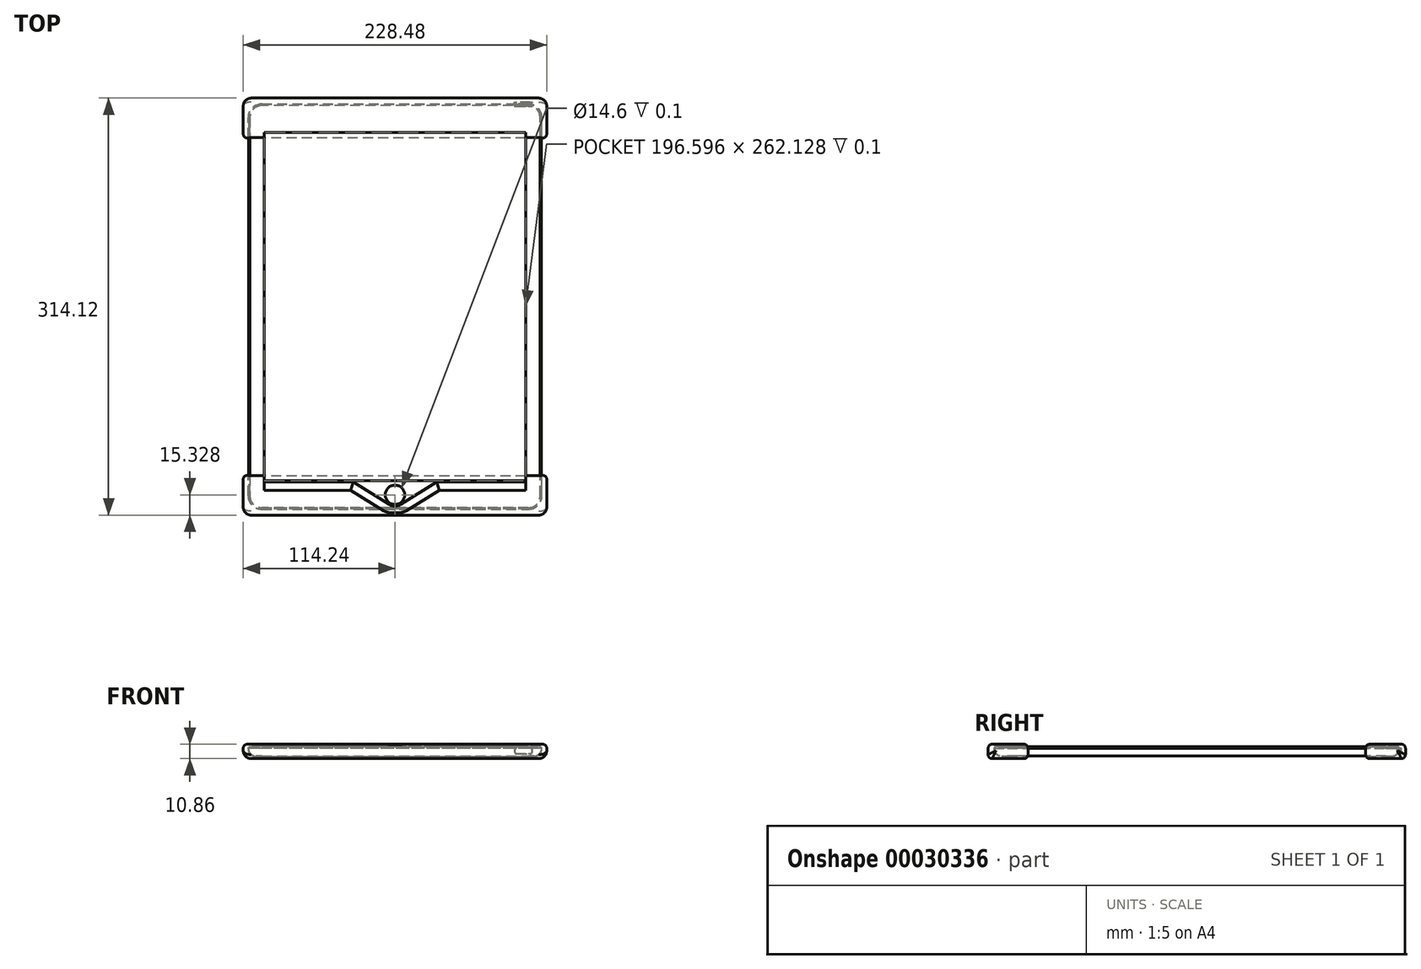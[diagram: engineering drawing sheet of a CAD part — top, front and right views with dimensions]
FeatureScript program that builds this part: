
annotation { "Feature Type Name" : "Feature", "Feature Type Description" : "" }
export const myFeature = defineFeature(function(context is Context, id is Id, definition is map)
    precondition{}
    {
        {
            var Q0;
            Q0=qCreatedBy(makeId("Top.planeOp"),FACE);
            var sketch = newSketch(context, id + "F0", { "sketchPlane" : qUnion([Q0])});
            skLineSegment(sketch, "E0.rect.bottom", {"start": v(-100.24, 152.4) * mm, "end": v(100.24, 152.4) * mm});
            skLineSegment(sketch, "E0.rect.top", {"start": v(-100.24, -152.4) * mm, "end": v(100.24, -152.4) * mm});
            skLineSegment(sketch, "E0.rect.left", {"start": v(-110.24, 142.4) * mm, "end": v(-110.24, -142.4) * mm});
            skLineSegment(sketch, "E0.rect.right", {"start": v(110.24, 142.4) * mm, "end": v(110.24, -142.4) * mm});
            skPoint(sketch, "E0.rect.middle", {"position": v(0, 0) * mm});
            skLineSegment(sketch, "E1.rect.bottom", {"start": v(98.3, 131.06) * mm, "end": v(-98.3, 131.06) * mm});
            skLineSegment(sketch, "E1.rect.top", {"start": v(98.3, -131.06) * mm, "end": v(-98.3, -131.06) * mm});
            skLineSegment(sketch, "E1.rect.left", {"start": v(98.3, 131.06) * mm, "end": v(98.3, -131.06) * mm});
            skLineSegment(sketch, "E1.rect.right", {"start": v(-98.3, 131.06) * mm, "end": v(-98.3, -131.06) * mm});
            skLineSegment(sketch, "E2", {"start": v(-98.3, 131.06) * mm, "end": v(-98.3, 0) * mm});
            skLineSegment(sketch, "E3", {"start": v(-98.3, 0) * mm, "end": v(-98.3, 65.53) * mm});
            skLineSegment(sketch, "E4", {"start": v(-98.3, 131.06) * mm, "end": v(-32.77, 131.06) * mm});
            skLineSegment(sketch, "E5", {"start": v(-32.77, 131.06) * mm, "end": v(32.77, 131.06) * mm});
            skLineSegment(sketch, "E6", {"start": v(32.77, 131.06) * mm, "end": v(98.3, 131.06) * mm});
            skLineSegment(sketch, "E7", {"start": v(-98.3, 131.06) * mm, "end": v(98.3, -131.06) * mm, "construction": true});
            skPoint(sketch, "E8.visualSharp", {"position": v(110.24, 152.4) * mm});
            skArc(sketch, "E8.filletArc", {"start": v(110.24, 142.4) * mm, "mid": v(107.3, 149.47) * mm, "end": v(100.24, 152.4) * mm});
            skPoint(sketch, "E9.visualSharp", {"position": v(110.24, -152.4) * mm});
            skArc(sketch, "E9.filletArc", {"start": v(100.24, -152.4) * mm, "mid": v(107.3, -149.47) * mm, "end": v(110.24, -142.4) * mm});
            skPoint(sketch, "E10.visualSharp", {"position": v(-110.24, -152.4) * mm});
            skArc(sketch, "E10.filletArc", {"start": v(-110.24, -142.4) * mm, "mid": v(-107.3, -149.47) * mm, "end": v(-100.24, -152.4) * mm});
            skPoint(sketch, "E11.visualSharp", {"position": v(-110.24, 152.4) * mm});
            skArc(sketch, "E11.filletArc", {"start": v(-100.24, 152.4) * mm, "mid": v(-107.3, 149.47) * mm, "end": v(-110.24, 142.4) * mm});
            skLineSegment(sketch, "E12", {"start": v(0, -131.06) * mm, "end": v(0, -152.4) * mm, "construction": true});
            skCircle(sketch, "E13", {"center": v(0, -141.73) * mm, "radius": 7.3 * mm});
            skLineSegment(sketch, "E14", {"start": v(-110.24, 0) * mm, "end": v(110.24, 0) * mm, "construction": true});
            skLineSegment(sketch, "E15", {"start": v(3.83, -147.95) * mm, "end": v(31.22, -131.06) * mm});
            skLineSegment(sketch, "E16.MirrorCS", {"start": v(-3.83, -147.95) * mm, "end": v(-31.22, -131.06) * mm});
            skSolve(sketch);
        }
        {
            var Q0;
            Q0=qSketchRegion(id+"F0",true);
            var Q1;
            Q1=makeQuery(id+"F0.imprint","IMPRINT",FACE,{"disambiguationData":[TD([[makeQuery(id+"F0.imprint","IMPRINT",EDGE,{"derivedFrom":sQuery(id+"F0.wireOp",EDGE,"E1.rect.top")}),-1.0]])]});
            var Q2;
            Q2=makeQuery(id+"F0.imprint","IMPRINT",FACE,{"disambiguationData":[TD([[makeQuery(id+"F0.imprint","IMPRINT",EDGE,{"derivedFrom":sQuery(id+"F0.wireOp",EDGE,"E13")}),1.0]])]});
            var Q3;
            {var subQ0=sQuery(id+"F0.wireOp",EDGE,"E15");Q3=makeQuery(id+"F0.imprint","IMPRINT",FACE,{"disambiguationData":[TD([[makeQuery(id+"F0.imprint","IMPRINT",EDGE,{"derivedFrom":subQ0}),1.0]])]});}
            extrude(context, id + "F1", {"entities" : qUnion([Q0, Q1, Q2, Q3]), "oppositeDirection" : true, "depth" : 6.86 * mm});
        }
        {
            var Q0;
            Q0=makeQuery(id+"F1.opExtrude","CAP_EDGE",EDGE,{"disambiguationData":[OSD([sQuery(id+"F0.wireOp",EDGE,"E0.rect.bottom")])],"isStart":false});
            fillet(context, id + "F2", {"entities" : qUnion([Q0]), "radius" : 5.6 * mm, "tangentPropagation" : true, "allowEdgeOverflow" : false});
        }
        {
            var Q0;
            Q0=makeQuery(id+"F1.opExtrude","CAP_EDGE",EDGE,{"disambiguationData":[OSD([sQuery(id+"F0.wireOp",EDGE,"E0.rect.bottom")])],"isStart":true});
            chamfer(context, id + "F3", {"entities" : qUnion([Q0]), "width" : 1 * mm, "tangentPropagation" : true});
        }
        {
            var Q0;
            Q0=qCreatedBy(makeId("Front.planeOp"),FACE);
            var Q1;
            Q1=sQuery(id+"F0.wireOp",VERTEX,"E7.end");
            cPlane(context, id + "F4", {"entities" : qUnion([Q0, Q1]), "cplaneType" : CPlaneType.PLANE_POINT, "offset" : 150 * mm, "width" : 150 * mm, "height" : 150 * mm});
        }
        {
            var Q0;
            Q0=qCreatedBy(id+"F4.planeOp",FACE);
            var sketch = newSketch(context, id + "F5", { "sketchPlane" : qUnion([Q0])});
            skLineSegment(sketch, "E17.bottom", {"start": v(-114.24, 2) * mm, "end": v(114.24, 2) * mm});
            skLineSegment(sketch, "E17.top", {"start": v(-114.24, -8.86) * mm, "end": v(114.24, -8.86) * mm});
            skLineSegment(sketch, "E17.left", {"start": v(-114.24, 2) * mm, "end": v(-114.24, -8.86) * mm});
            skLineSegment(sketch, "E17.right", {"start": v(114.24, 2) * mm, "end": v(114.24, -8.86) * mm});
            skPoint(sketch, "E17.middle", {"position": v(0, -3.43) * mm});
            skSolve(sketch);
        }
        {
            var Q0;
            Q0=makeQuery(id+"F5.imprint","IMPRINT",FACE,{"disambiguationData":[TD([[makeQuery(id+"F5.imprint","IMPRINT",EDGE,{"derivedFrom":sQuery(id+"F5.wireOp",EDGE,"E17.bottom")}),-1.0]])]});
            extrude(context, id + "F6", {"entities" : qUnion([Q0]), "depth" : 26 * mm, "hasSecondDirection" : true, "secondDirectionOppositeDirection" : true, "secondDirectionDepth" : 4 * mm});
        }
        {
            var Q0;
            Q0=makeQuery(id+"F6.opExtrude","SWEPT_EDGE",EDGE,{"disambiguationData":[OSD([sQuery(id+"F5.wireOp",EDGE,"E17.top"),sQuery(id+"F5.wireOp",EDGE,"E17.left")])]});
            var Q1;
            Q1=makeQuery(id+"F6.opExtrude","SWEPT_EDGE",EDGE,{"disambiguationData":[OSD([sQuery(id+"F5.wireOp",EDGE,"E17.top"),sQuery(id+"F5.wireOp",EDGE,"E17.right")])]});
            var Q2;
            Q2=makeQuery(id+"F6.opExtrude","CAP_EDGE",EDGE,{"disambiguationData":[OSD([sQuery(id+"F5.wireOp",EDGE,"E17.left")])],"isStart":false});
            var Q3;
            Q3=makeQuery(id+"F6.opExtrude","CAP_EDGE",EDGE,{"disambiguationData":[OSD([sQuery(id+"F5.wireOp",EDGE,"E17.right")])],"isStart":false});
            fillet(context, id + "F7", {"entities" : qUnion([Q0, Q1, Q2, Q3]), "radius" : 6 * mm, "tangentPropagation" : true, "allowEdgeOverflow" : false});
        }
        {
            var Q0;
            Q0=makeQuery(id+"F6.opExtrude","CAP_EDGE",EDGE,{"disambiguationData":[OSD([sQuery(id+"F5.wireOp",EDGE,"E17.bottom")])],"isStart":false});
            var Q1;
            {var subQ0=sQuery(id+"F5.wireOp",EDGE,"E17.left");var subQ1=sQuery(id+"F5.wireOp",EDGE,"E17.top");Q1=makeQuery(id+"F7.opFillet","BLEND_EDGE",EDGE,{"blendedFrom":[makeQuery(id+"F6.opExtrude","SWEPT_EDGE",EDGE,{"disambiguationData":[OSD([subQ1,subQ0])]}),makeQuery(id+"F6.opExtrude","CAP_FACE",FACE,{"disambiguationData":[OSD([sQuery(id+"F5.wireOp",EDGE,"E17.bottom"),subQ1,subQ0,sQuery(id+"F5.wireOp",EDGE,"E17.right")])],"isStart":false})],"blendedInto":[makeQuery(id+"F6.opExtrude","CAP_FACE",FACE,{"disambiguationData":[OSD([sQuery(id+"F5.wireOp",EDGE,"E17.bottom"),subQ1,subQ0,sQuery(id+"F5.wireOp",EDGE,"E17.right")])],"isStart":false})]});}
            var Q2;
            Q2=makeQuery(id+"F6.opExtrude","CAP_EDGE",EDGE,{"disambiguationData":[OSD([sQuery(id+"F5.wireOp",EDGE,"E17.top")])],"isStart":false});
            var Q3;
            {var subQ0=sQuery(id+"F5.wireOp",EDGE,"E17.right");var subQ1=sQuery(id+"F5.wireOp",EDGE,"E17.top");Q3=makeQuery(id+"F7.opFillet","BLEND_EDGE",EDGE,{"blendedFrom":[makeQuery(id+"F6.opExtrude","SWEPT_EDGE",EDGE,{"disambiguationData":[OSD([subQ1,subQ0])]}),makeQuery(id+"F6.opExtrude","CAP_FACE",FACE,{"disambiguationData":[OSD([sQuery(id+"F5.wireOp",EDGE,"E17.bottom"),subQ1,sQuery(id+"F5.wireOp",EDGE,"E17.left"),subQ0])],"isStart":false})],"blendedInto":[makeQuery(id+"F6.opExtrude","CAP_FACE",FACE,{"disambiguationData":[OSD([sQuery(id+"F5.wireOp",EDGE,"E17.bottom"),subQ1,sQuery(id+"F5.wireOp",EDGE,"E17.left"),subQ0])],"isStart":false})]});}
            var Q4;
            Q4=makeQuery(id+"F6.opExtrude","CAP_EDGE",EDGE,{"disambiguationData":[OSD([sQuery(id+"F5.wireOp",EDGE,"E17.right")])],"isStart":false});
            var Q5;
            Q5=makeQuery(id+"F6.opExtrude","SWEPT_EDGE",EDGE,{"disambiguationData":[OSD([sQuery(id+"F5.wireOp",EDGE,"E17.bottom"),sQuery(id+"F5.wireOp",EDGE,"E17.right")])]});
            var Q6;
            Q6=makeQuery(id+"F6.opExtrude","SWEPT_EDGE",EDGE,{"disambiguationData":[OSD([sQuery(id+"F5.wireOp",EDGE,"E17.bottom"),sQuery(id+"F5.wireOp",EDGE,"E17.left")])]});
            var Q7;
            Q7=makeQuery(id+"F6.opExtrude","CAP_EDGE",EDGE,{"disambiguationData":[OSD([sQuery(id+"F5.wireOp",EDGE,"E17.left")])],"isStart":false});
            var Q8;
            Q8=makeQuery(id+"F6.opExtrude","CAP_EDGE",EDGE,{"disambiguationData":[OSD([sQuery(id+"F5.wireOp",EDGE,"E17.left")])],"isStart":true});
            var Q9;
            Q9=makeQuery(id+"F6.opExtrude","CAP_EDGE",EDGE,{"disambiguationData":[OSD([sQuery(id+"F5.wireOp",EDGE,"E17.bottom")])],"isStart":true});
            fillet(context, id + "F8", {"entities" : qUnion([Q0, Q1, Q2, Q3, Q4, Q5, Q6, Q7, Q8, Q9]), "radius" : 3 * mm, "tangentPropagation" : true, "allowEdgeOverflow" : false});
        }
        {
            var Q0;
            Q0=makeQuery(id+"F6.opExtrude","SWEPT_BODY",BODY,{"disambiguationData":[OSD([sQuery(id+"F5.wireOp",EDGE,"E17.bottom"),sQuery(id+"F5.wireOp",EDGE,"E17.top"),sQuery(id+"F5.wireOp",EDGE,"E17.left"),sQuery(id+"F5.wireOp",EDGE,"E17.right")])]});
            var Q1;
            Q1=qCreatedBy(makeId("Front.planeOp"),FACE);
            mirror(context, id + "F9", {"entities" : qUnion([Q0]), "mirrorPlane" : qUnion([Q1])});
        }
        {
            var Q0;
            Q0=makeQuery(id+"F0.imprint","IMPRINT",FACE,{"disambiguationData":[TD([[makeQuery(id+"F0.imprint","IMPRINT",EDGE,{"derivedFrom":sQuery(id+"F0.wireOp",EDGE,"E1.rect.top")}),-1.0]])]});
            var Q1;
            Q1=makeQuery(id+"F0.imprint","IMPRINT",FACE,{"disambiguationData":[TD([[makeQuery(id+"F0.imprint","IMPRINT",EDGE,{"derivedFrom":sQuery(id+"F0.wireOp",EDGE,"E13")}),1.0]])]});
            var Q2;
            {var subQ0=sQuery(id+"F0.wireOp",EDGE,"E15");Q2=makeQuery(id+"F0.imprint","IMPRINT",FACE,{"disambiguationData":[TD([[makeQuery(id+"F0.imprint","IMPRINT",EDGE,{"derivedFrom":subQ0}),1.0]])]});}
            extrude(context, id + "F10", {"entities" : qUnion([Q0, Q1, Q2]), "operationType" : NewBodyOperationType.REMOVE, "depth" : 25 * mm});
        }
        {
            var Q0;
            Q0=makeQuery(id+"F10.boolean.opBoolean","INTERSECT",EDGE,{"derivedFrom":[makeQuery(id+"F6.opExtrude","SWEPT_FACE",FACE,{"disambiguationData":[OSD([sQuery(id+"F5.wireOp",EDGE,"E17.bottom")])]}),makeQuery(id+"F10.opExtrude","SWEPT_FACE",FACE,{"disambiguationData":[OSD([sQuery(id+"F0.wireOp",EDGE,"E1.rect.top")])]})]});
            var Q1;
            Q1=makeQuery(id+"F10.boolean.opBoolean","INTERSECT",EDGE,{"derivedFrom":[makeQuery(id+"F6.opExtrude","SWEPT_FACE",FACE,{"disambiguationData":[OSD([sQuery(id+"F5.wireOp",EDGE,"E17.bottom")])]}),makeQuery(id+"F10.opExtrude","SWEPT_FACE",FACE,{"disambiguationData":[OSD([sQuery(id+"F0.wireOp",EDGE,"E13")])]})]});
            chamfer(context, id + "F11", {"entities" : qUnion([Q0, Q1]), "chamferType" : ChamferType.OFFSET_ANGLE, "width" : 2 * mm, "oppositeDirection" : false, "angle" : 75 * degree, "tangentPropagation" : true});
        }
        {
            var Q0;
            Q0=makeQuery(id+"F1.opExtrude","SWEPT_BODY",BODY,{"disambiguationData":[OSD([sQuery(id+"F0.wireOp",EDGE,"E0.rect.bottom"),sQuery(id+"F0.wireOp",EDGE,"E0.rect.top"),sQuery(id+"F0.wireOp",EDGE,"E0.rect.left"),sQuery(id+"F0.wireOp",EDGE,"E0.rect.right"),sQuery(id+"F0.wireOp",EDGE,"E8.filletArc"),sQuery(id+"F0.wireOp",EDGE,"E9.filletArc"),sQuery(id+"F0.wireOp",EDGE,"E10.filletArc"),sQuery(id+"F0.wireOp",EDGE,"E11.filletArc")])]});
            var Q1;
            Q1=makeQuery(id+"F6.opExtrude","SWEPT_BODY",BODY,{"disambiguationData":[OSD([sQuery(id+"F5.wireOp",EDGE,"E17.bottom"),sQuery(id+"F5.wireOp",EDGE,"E17.top"),sQuery(id+"F5.wireOp",EDGE,"E17.left"),sQuery(id+"F5.wireOp",EDGE,"E17.right")])]});
            var Q2;
            Q2=makeQuery(id+"F9.opPattern","COPY",BODY,{"derivedFrom":makeQuery(id+"F6.opExtrude","SWEPT_BODY",BODY,{"disambiguationData":[OSD([sQuery(id+"F5.wireOp",EDGE,"E17.bottom"),sQuery(id+"F5.wireOp",EDGE,"E17.top"),sQuery(id+"F5.wireOp",EDGE,"E17.left"),sQuery(id+"F5.wireOp",EDGE,"E17.right")])]}),"instanceName":"1"});
            booleanBodies(context, id + "F12", {"operationType" : BooleanOperationType.SUBTRACTION, "tools" : qUnion([Q0]), "targets" : qUnion([Q1, Q2]), "offset" : true, "offsetAll" : true, "offsetDistance" : .3 * mm, "keepTools" : true});
        }
        {
            var Q0;
            Q0=makeQuery(id+"F1.opExtrude","SWEPT_FACE",FACE,{"disambiguationData":[OSD([sQuery(id+"F0.wireOp",EDGE,"E0.rect.bottom")])]});
            var sketch = newSketch(context, id + "F13", { "sketchPlane" : qUnion([Q0])});
            skLineSegment(sketch, "E18.bottom", {"start": v(-91.74, -1.1) * mm, "end": v(-101.74, -1.1) * mm});
            skLineSegment(sketch, "E18.top", {"start": v(-91.74, -5.1) * mm, "end": v(-101.74, -5.1) * mm});
            skLineSegment(sketch, "E18.left", {"start": v(-90.24, -2.6) * mm, "end": v(-90.24, -3.6) * mm});
            skLineSegment(sketch, "E18.right", {"start": v(-103.24, -2.6) * mm, "end": v(-103.24, -3.6) * mm});
            skPoint(sketch, "E18.middle", {"position": v(-96.74, -3.1) * mm});
            skPoint(sketch, "E19.visualSharp", {"position": v(-103.24, -1.1) * mm});
            skArc(sketch, "E19.filletArc", {"start": v(-101.74, -1.1) * mm, "mid": v(-102.8, -1.54) * mm, "end": v(-103.24, -2.6) * mm});
            skPoint(sketch, "E20.visualSharp", {"position": v(-90.24, -1.1) * mm});
            skArc(sketch, "E20.filletArc", {"start": v(-90.24, -2.6) * mm, "mid": v(-90.68, -1.54) * mm, "end": v(-91.74, -1.1) * mm});
            skPoint(sketch, "E21.visualSharp", {"position": v(-90.24, -5.1) * mm});
            skArc(sketch, "E21.filletArc", {"start": v(-91.74, -5.1) * mm, "mid": v(-90.68, -4.66) * mm, "end": v(-90.24, -3.6) * mm});
            skPoint(sketch, "E22.visualSharp", {"position": v(-103.24, -5.1) * mm});
            skArc(sketch, "E22.filletArc", {"start": v(-103.24, -3.6) * mm, "mid": v(-102.8, -4.66) * mm, "end": v(-101.74, -5.1) * mm});
            skSolve(sketch);
        }
        {
            var Q0;
            Q0=makeQuery(id+"F13.imprint","IMPRINT",FACE,{"disambiguationData":[TD([[makeQuery(id+"F13.imprint","IMPRINT",EDGE,{"derivedFrom":sQuery(id+"F13.wireOp",EDGE,"E18.bottom")}),1.0]])]});
            var Q1;
            Q1=makeQuery(id+"F13.imprint","IMPRINT",FACE,{"disambiguationData":[TD([[makeQuery(id+"F13.imprint","IMPRINT",EDGE,{"derivedFrom":sQuery(id+"F13.wireOp",EDGE,"E18.top")}),-1.0]])]});
            extrude(context, id + "F14", {"entities" : qUnion([Q0, Q1]), "operationType" : NewBodyOperationType.REMOVE, "endBound" : BoundingType.SYMMETRIC, "depth" : 3 * mm, "hasDraft" : true, "draftAngle" : 10 * degree});
        }
        {
            var Q0;
            {var subQ0=sQuery(id+"F0.wireOp",EDGE,"E1.rect.left");Q0=makeQuery(id+"F0.imprint","IMPRINT",FACE,{"disambiguationData":[TD([[makeQuery(id+"F0.imprint","IMPRINT",EDGE,{"derivedFrom":subQ0}),-1.0]])]});}
            var Q1;
            {var subQ0=sQuery(id+"F0.wireOp",EDGE,"E13");var subQ1=makeQuery(id+"F0.imprint","INTERSECT",VERTEX,{"derivedFrom":[subQ0,sQuery(id+"F0.wireOp",EDGE,"E15")]});Q1=makeQuery(id+"F0.imprint","IMPRINT",FACE,{"disambiguationData":[TD([[makeQuery(id+"F0.imprint","IMPRINT",EDGE,{"disambiguationData":[TD([[subQ1,1.0]])],"derivedFrom":subQ0}),1.0]])]});}
            extrude(context, id + "F15", {"entities" : qUnion([Q0, Q1]), "operationType" : NewBodyOperationType.REMOVE, "oppositeDirection" : true, "depth" : .1 * mm});
        }
    });
